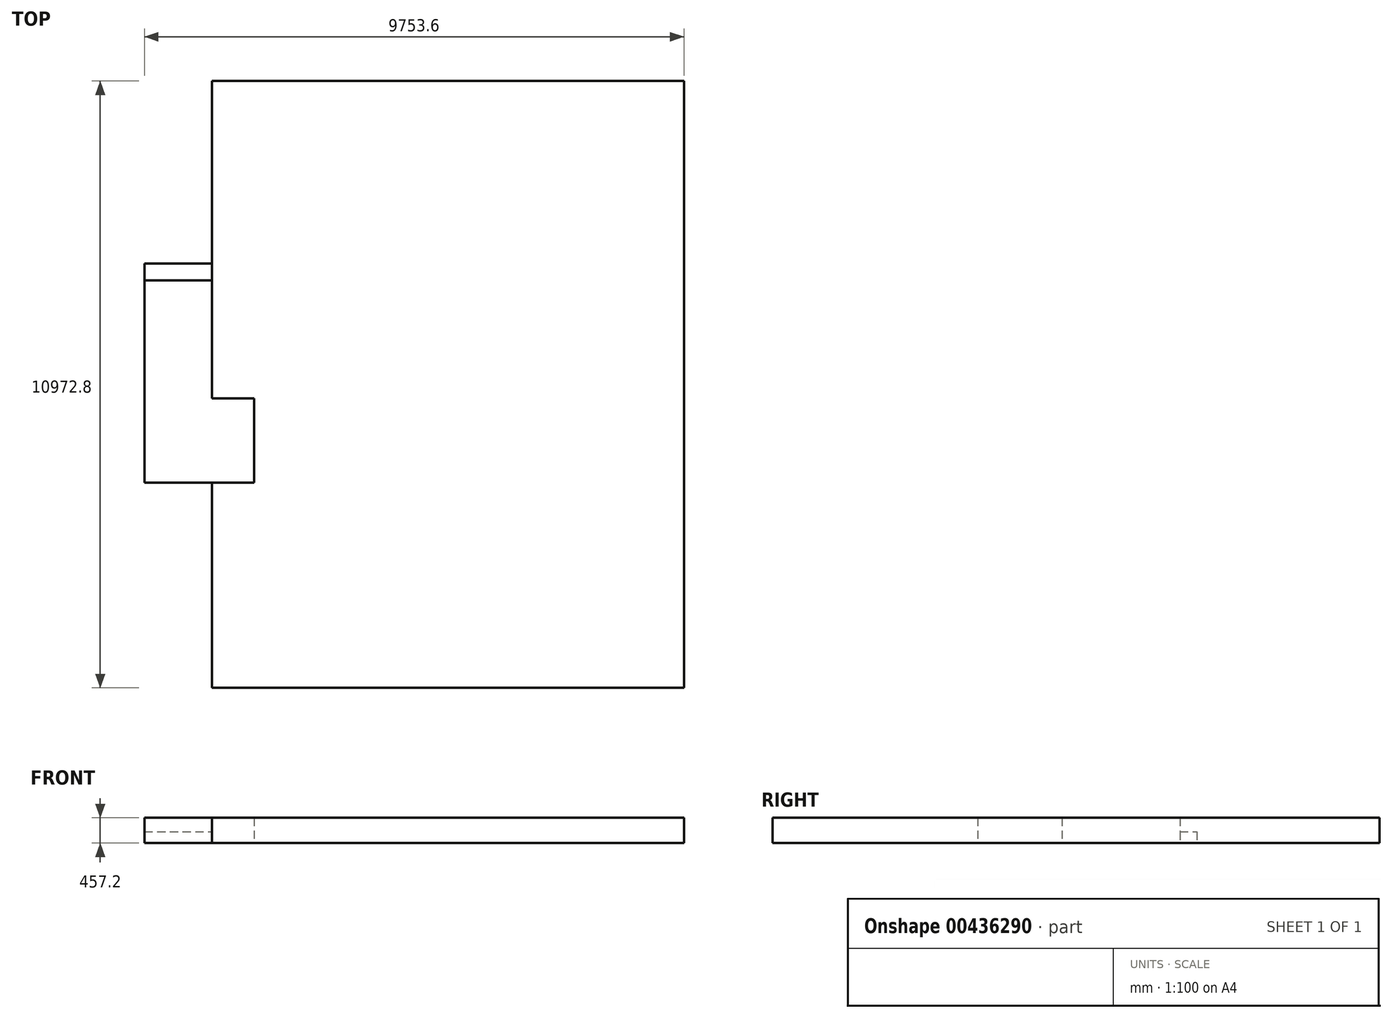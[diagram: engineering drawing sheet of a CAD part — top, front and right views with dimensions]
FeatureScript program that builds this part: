
annotation { "Feature Type Name" : "Feature", "Feature Type Description" : "" }
export const myFeature = defineFeature(function(context is Context, id is Id, definition is map)
    precondition{}
    {
        {
            var Q0;
            Q0=qCreatedBy(makeId("Top.planeOp"),FACE);
            var sketch = newSketch(context, id + "F0", { "sketchPlane" : qUnion([Q0])});
            skLineSegment(sketch, "E0", {"start": v(0, 0) * mm, "end": v(-1524, 0) * mm, "construction": true});
            skLineSegment(sketch, "E1", {"start": v(-1524, 0) * mm, "end": v(0, 0) * mm, "construction": true});
            skLineSegment(sketch, "E2", {"start": v(0, 0) * mm, "end": v(0, 4267.2) * mm, "construction": true});
            skLineSegment(sketch, "E3", {"start": v(-1524, 4267.2) * mm, "end": v(-10058.4, 4267.2) * mm});
            skLineSegment(sketch, "E4", {"start": v(-1524, 4267.2) * mm, "end": v(-1524, 15240) * mm});
            skLineSegment(sketch, "E5", {"start": v(-10058.4, 4267.2) * mm, "end": v(-10058.4, 7975.4) * mm});
            skLineSegment(sketch, "E6", {"start": v(-10058.4, 7975.4) * mm, "end": v(-9296.4, 7975.4) * mm});
            skLineSegment(sketch, "E7", {"start": v(-9296.4, 7975.4) * mm, "end": v(-9296.4, 9499.4) * mm});
            skLineSegment(sketch, "E8", {"start": v(-9296.4, 9499.4) * mm, "end": v(-10058.4, 9499.4) * mm});
            skLineSegment(sketch, "E9", {"start": v(-10058.4, 9499.4) * mm, "end": v(-10058.4, 15240) * mm});
            skLineSegment(sketch, "E10", {"start": v(-10058.4, 15240) * mm, "end": v(-1524, 15240) * mm});
            skLineSegment(sketch, "E11", {"start": v(-10058.4, 7975.4) * mm, "end": v(-11277.6, 7975.4) * mm});
            skLineSegment(sketch, "E12", {"start": v(-11277.6, 7975.4) * mm, "end": v(-11277.6, 11633) * mm});
            skLineSegment(sketch, "E13", {"start": v(-11277.6, 11633) * mm, "end": v(-10058.4, 11633) * mm});
            skLineSegment(sketch, "E14", {"start": v(-11277.6, 11633) * mm, "end": v(-11277.6, 11937.8) * mm});
            skLineSegment(sketch, "E15", {"start": v(-11277.6, 11937.8) * mm, "end": v(-10058.4, 11937.8) * mm});
            skSolve(sketch);
        }
        {
            var Q0;
            Q0=makeQuery(id+"F0.imprint","IMPRINT",FACE,{"disambiguationData":[TD([[makeQuery(id+"F0.imprint","IMPRINT",EDGE,{"derivedFrom":sQuery(id+"F0.wireOp",EDGE,"E3")}),-1.0]])]});
            extrude(context, id + "F1", {"entities" : qUnion([Q0]), "depth" : 457.2 * mm});
        }
        {
            var Q0;
            Q0=makeQuery(id+"F0.imprint","IMPRINT",FACE,{"disambiguationData":[TD([[makeQuery(id+"F0.imprint","IMPRINT",EDGE,{"derivedFrom":sQuery(id+"F0.wireOp",EDGE,"E6")}),1.0]])]});
            extrude(context, id + "F2", {"entities" : qUnion([Q0]), "depth" : 457.2 * mm});
        }
        {
            var Q0;
            {var subQ0=sQuery(id+"F0.wireOp",EDGE,"E13");Q0=makeQuery(id+"F0.imprint","IMPRINT",FACE,{"disambiguationData":[TD([[makeQuery(id+"F0.imprint","IMPRINT",EDGE,{"derivedFrom":subQ0}),1.0]])]});}
            extrude(context, id + "F3", {"entities" : qUnion([Q0]), "depth" : 203 * mm});
        }
    });
